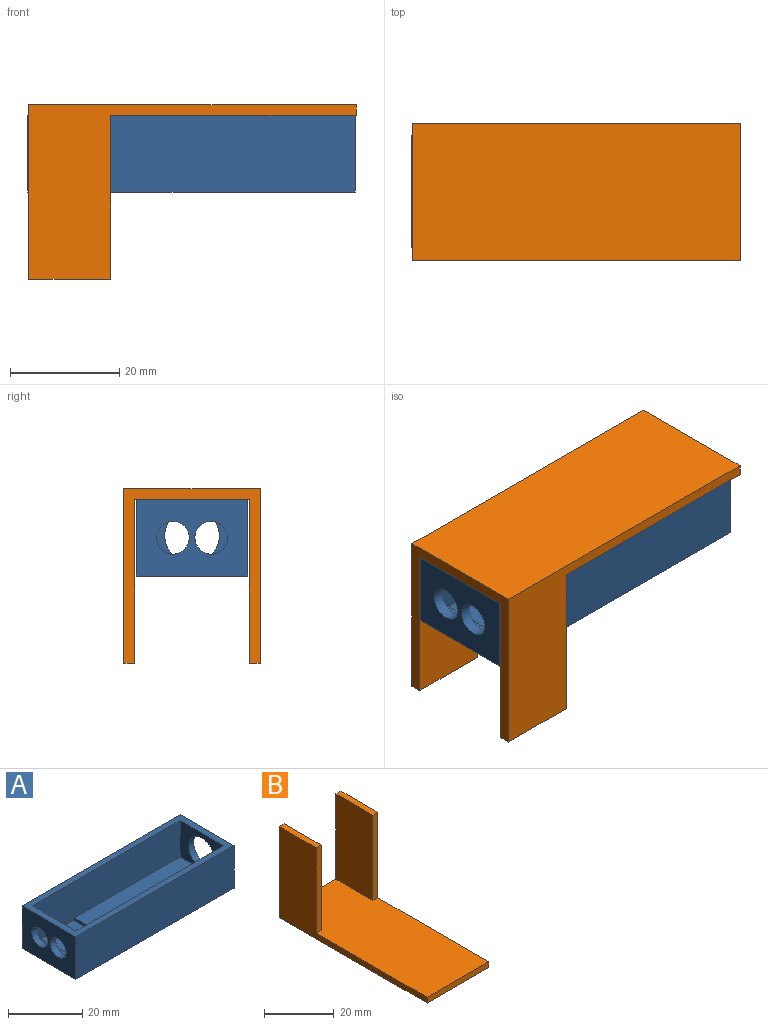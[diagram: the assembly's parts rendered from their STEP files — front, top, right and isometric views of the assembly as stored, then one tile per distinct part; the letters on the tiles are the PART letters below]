
ASSEMBLY  parts=2 mates=1
PART A: 24 faces, bbox 60x20.5x14 mm
  f0: plane 17.45x13.23mm, normal (0,0,1), area 211.5mm2, adj f17,f18,f19,f20,f22,f23
  f1: plane 60x20.5mm, normal (0,0,-1), area 1210.8mm2, adj f3,f5,f6,f10,f22,f23
  f2: plane 16.5x2.81mm, normal (0,0,1), area 46.4mm2, adj f4,f7,f9,f17
  f3: plane 20.5x14mm, normal (-1,0,0), area 230.5mm2, adj f1,f5,f6,f11,f14,f15
  f4: plane 16.5x12mm, normal (1,0,0), area 141.5mm2, adj f2,f7,f9,f11,f14,f15
  f5: plane 60x14mm, normal (0,1,0), area 840mm2, adj f1,f3,f10,f11
  f6: plane 60x14mm, normal (0,-1,0), area 840mm2, adj f1,f3,f10,f11
  f7: plane 56x12mm, normal (0,-1,0), area 672mm2, adj f2,f4,f8,f11,f12,f16
  f8: plane 16.5x12mm, normal (-1,0,0), area 119.5mm2, adj f7,f9,f11,f12,f13
  f9: plane 56x12mm, normal (0,1,0), area 672mm2, adj f2,f4,f8,f11,f12,f21
  f10: plane 20.5x14mm, normal (1,0,0), area 208.5mm2, adj f1,f5,f6,f11,f13
  f11: plane 60x20.5mm, normal (0,0,1), area 306mm2, adj f3,f4,f5,f6,f7,f8,f9,f10
  f12: plane 39.96x16.5mm, normal (0,0,1), area 659.4mm2, adj f7,f8,f9,f19
  f13: cylinder r=5mm len=10mm, axis (1,0,0), area 62.8mm2, adj f8,f10
  f14: cylinder r=3mm len=6mm, axis (-1,0,0), area 37.7mm2, adj f3,f4
  f15: cylinder r=3mm len=6mm, axis (-1,0,0), area 37.7mm2, adj f3,f4
  f16: plane 13.23x0.47mm, normal (0,0,-1), area 6.3mm2, adj f7,f17,f19,f20
  f17: plane 17.45x1mm, normal (1,0,0), area 17.4mm2, adj f0,f2,f16,f18,f20,f21
  f18: plane 13.23x1mm, normal (0,1,0), area 13.2mm2, adj f0,f17,f19,f21
  f19: plane 17.45x1mm, normal (-1,0,0), area 17.4mm2, adj f0,f12,f16,f18,f20,f21
  f20: plane 13.23x1mm, normal (0,-1,0), area 13.2mm2, adj f0,f16,f17,f19
  f21: plane 13.23x0.47mm, normal (0,0,-1), area 6.3mm2, adj f9,f17,f18,f19
  f22: cylinder r=1.75mm len=3.5mm, axis (0,0,1), area 11mm2, adj f0,f1
  f23: cylinder r=1.75mm len=3.5mm, axis (0,0,1), area 11mm2, adj f0,f1
PART B: 12 faces, bbox 25x60x32 mm
  f0: plane 60x25mm, normal (0,0,1), area 1440mm2, adj f1,f2,f3,f4,f6,f7,f9,f10
  f1: plane 32x25mm, normal (0,1,0), area 170mm2, adj f0,f2,f4,f5,f7,f8,f9,f11
  f2: plane 60x32mm, normal (-1,0,0), area 570mm2, adj f0,f1,f3,f5,f6,f8
  f3: plane 25x2mm, normal (0,-1,0), area 50mm2, adj f0,f2,f4,f5
  f4: plane 60x32mm, normal (1,0,0), area 570mm2, adj f0,f1,f3,f5,f10,f11
  f5: plane 60x25mm, normal (0,0,-1), area 1500mm2, adj f1,f2,f3,f4
  f6: plane 30x2mm, normal (0,-1,0), area 60mm2, adj f0,f2,f7,f8
  f7: plane 30x15mm, normal (1,0,0), area 450mm2, adj f0,f1,f6,f8
  f8: plane 15x2mm, normal (0,0,1), area 30mm2, adj f1,f2,f6,f7
  f9: plane 30x15mm, normal (-1,0,0), area 450mm2, adj f0,f1,f10,f11
  f10: plane 30x2mm, normal (0,-1,0), area 60mm2, adj f0,f4,f9,f11
  f11: plane 15x2mm, normal (0,0,1), area 30mm2, adj f1,f4,f9,f10
PLACE A t=(-0.3,0,0)mm
PLACE B rot(axis=(0.71,-0.71,0),180deg) t=(-0.13,1.09,16)mm
MATE planar B.f0 <-> A.f11  axis (0,0,-1) through (0.81,0.01,14)mm
